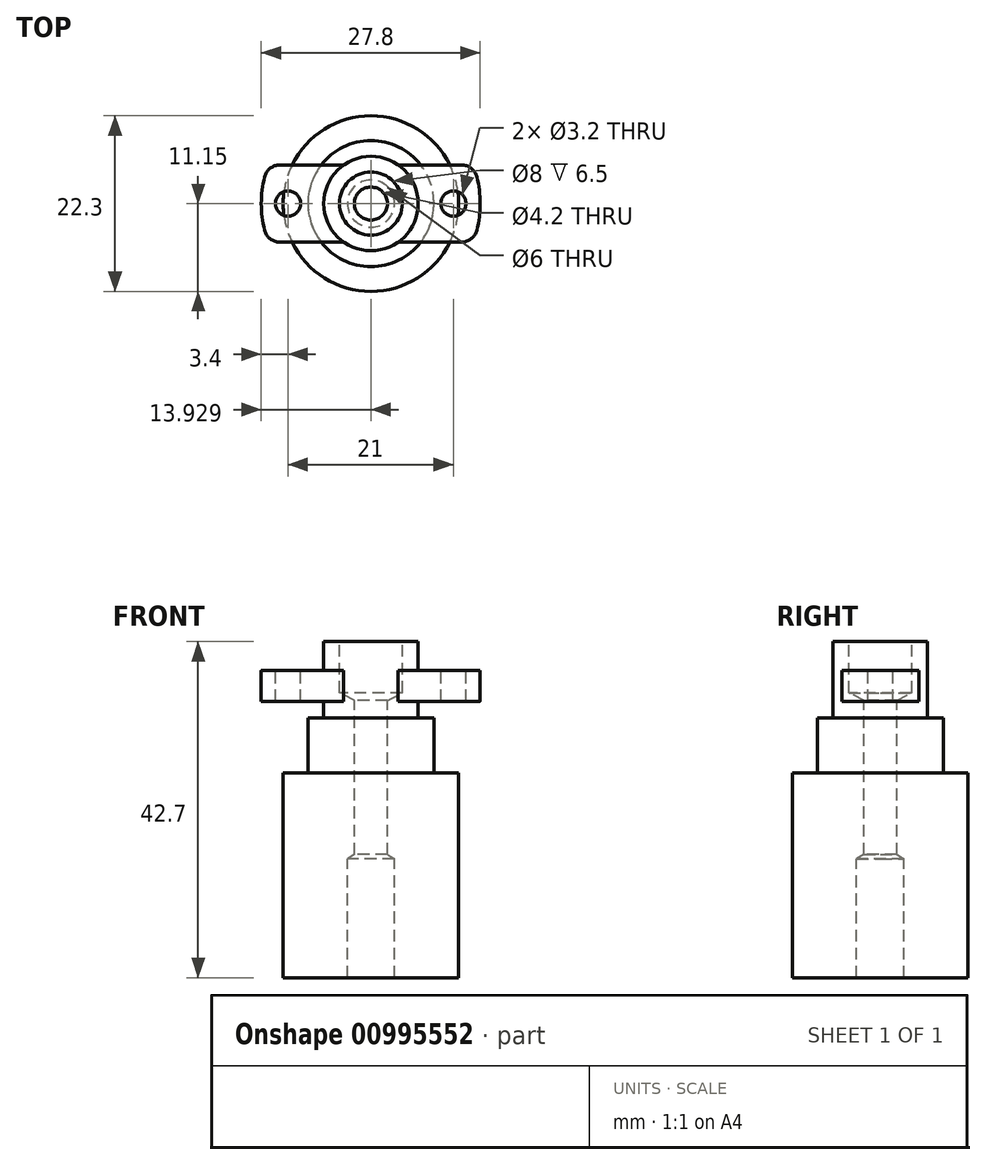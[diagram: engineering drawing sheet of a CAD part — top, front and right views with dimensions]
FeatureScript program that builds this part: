
annotation { "Feature Type Name" : "Feature", "Feature Type Description" : "" }
export const myFeature = defineFeature(function(context is Context, id is Id, definition is map)
    precondition{}
    {
        {
            var Q0;
            Q0=qCreatedBy(makeId("Front.planeOp"),FACE);
            var sketch = newSketch(context, id + "F0", { "sketchPlane" : qUnion([Q0])});
            skLineSegment(sketch, "E0", {"start": v(0.03, 24.7) * mm, "end": v(0.03, -18) * mm, "construction": true});
            skLineSegment(sketch, "E1", {"start": v(3.03, -18) * mm, "end": v(11.18, -18) * mm});
            skLineSegment(sketch, "E2", {"start": v(11.18, -18) * mm, "end": v(11.18, 8) * mm});
            skLineSegment(sketch, "E3", {"start": v(11.18, 8) * mm, "end": v(8.03, 8) * mm});
            skLineSegment(sketch, "E4", {"start": v(8.03, 8) * mm, "end": v(8.03, 15) * mm});
            skLineSegment(sketch, "E5", {"start": v(8.03, 15) * mm, "end": v(6.03, 15) * mm});
            skLineSegment(sketch, "E6", {"start": v(6.03, 15) * mm, "end": v(6.03, 21) * mm});
            skLineSegment(sketch, "E7", {"start": v(8.03, 21) * mm, "end": v(8.03, 24.7) * mm, "construction": true});
            skLineSegment(sketch, "E8", {"start": v(8.03, 24.7) * mm, "end": v(6.03, 24.7) * mm, "construction": true});
            skLineSegment(sketch, "E9", {"start": v(4.03, 24.7) * mm, "end": v(4.03, 18.2) * mm});
            skLineSegment(sketch, "E10", {"start": v(4.03, 18.2) * mm, "end": v(2.13, 17.18) * mm});
            skLineSegment(sketch, "E11", {"start": v(2.13, 17.18) * mm, "end": v(2.13, -2.36) * mm});
            skLineSegment(sketch, "E12", {"start": v(2.13, -2.36) * mm, "end": v(3.03, -2.9) * mm});
            skLineSegment(sketch, "E13", {"start": v(3.03, -2.9) * mm, "end": v(3.03, -18) * mm});
            skLineSegment(sketch, "E14", {"start": v(6.03, 21) * mm, "end": v(6.03, 24.7) * mm});
            skLineSegment(sketch, "E15", {"start": v(4.03, 24.7) * mm, "end": v(6.03, 24.7) * mm});
            skSolve(sketch);
        }
        {
            var Q0;
            Q0=makeQuery(id+"F0.imprint","IMPRINT",FACE,{"disambiguationData":[TD([[makeQuery(id+"F0.imprint","IMPRINT",EDGE,{"derivedFrom":sQuery(id+"F0.wireOp",EDGE,"E1")}),1.0]])]});
            var Q1;
            Q1=sQuery(id+"F0.wireOp",EDGE,"E0");
            revolve(context, id + "F1", {"surfaceOperationType" : NewSurfaceOperationType.NEW, "entities" : qUnion([Q0]), "axis" : qUnion([Q1]), "revolveType" : RevolveType.FULL});
        }
        {
            var Q0;
            Q0=makeQuery(id+"F1.opRevolve","SWEPT_FACE",FACE,{"disambiguationData":[OSD([sQuery(id+"F0.wireOp",EDGE,"E15")])]});
            cPlane(context, id + "F2", {"entities" : qUnion([Q0]), "cplaneType" : CPlaneType.OFFSET, "offset" : 3.7 * mm, "oppositeDirection" : true, "width" : 150 * mm, "height" : 150 * mm});
        }
        {
            var Q0;
            Q0=qCreatedBy(id+"F2.planeOp",FACE);
            var sketch = newSketch(context, id + "F3", { "sketchPlane" : qUnion([Q0])});
            skArc(sketch, "E16", {"start": v(-13.48, 3.39) * mm, "mid": v(-13.9, 0) * mm, "end": v(-13.48, -3.39) * mm});
            skLineSegment(sketch, "E17", {"start": v(-13.9, 0) * mm, "end": v(14.8, 0) * mm, "construction": true});
            skLineSegment(sketch, "E18.0", {"start": v(-11.54, -4.9) * mm, "end": v(11.54, -4.9) * mm});
            skLineSegment(sketch, "E19.0", {"start": v(-11.54, 4.9) * mm, "end": v(11.54, 4.9) * mm});
            skArc(sketch, "E20.trimOffspring", {"start": v(13.48, -3.39) * mm, "mid": v(13.9, 0) * mm, "end": v(13.48, 3.39) * mm});
            skPoint(sketch, "E21.visualSharp", {"position": v(-13, 4.9) * mm});
            skArc(sketch, "E21.filletArc", {"start": v(-11.54, 4.9) * mm, "mid": v(-12.77, 4.48) * mm, "end": v(-13.48, 3.39) * mm});
            skPoint(sketch, "E22.visualSharp", {"position": v(13, 4.9) * mm});
            skArc(sketch, "E22.filletArc", {"start": v(13.48, 3.39) * mm, "mid": v(12.77, 4.48) * mm, "end": v(11.54, 4.9) * mm});
            skPoint(sketch, "E23.visualSharp", {"position": v(13, -4.9) * mm});
            skArc(sketch, "E23.filletArc", {"start": v(11.54, -4.9) * mm, "mid": v(12.77, -4.48) * mm, "end": v(13.48, -3.39) * mm});
            skPoint(sketch, "E24.visualSharp", {"position": v(-13, -4.9) * mm});
            skArc(sketch, "E24.filletArc", {"start": v(-13.48, -3.39) * mm, "mid": v(-12.77, -4.48) * mm, "end": v(-11.54, -4.9) * mm});
            skCircle(sketch, "E25.0", {"center": v(0.03, 0) * mm, "radius": 4 * mm});
            skSolve(sketch);
        }
        {
            var Q0;
            Q0 = qSketchRegion(id + "F3", true);
            extrude(context, id + "F4", {"entities" : qUnion([Q0]), "operationType" : NewBodyOperationType.ADD, "oppositeDirection" : true, "depth" : 3.9 * mm, "offsetDistance" : 25 * mm});
        }
        {
            var Q0;
            {var subQ0=sQuery(id+"F3.wireOp",EDGE,"E18.0");var subQ1=sQuery(id+"F3.wireOp",EDGE,"E16");var subQ2=sQuery(id+"F3.wireOp",EDGE,"E19.0");var subQ3=sQuery(id+"F3.wireOp",EDGE,"E24.filletArc");var subQ4=sQuery(id+"F3.wireOp",EDGE,"E21.filletArc");Q0=makeQuery(id+"F4.boolean.opBoolean","SPLIT",FACE,{"disambiguationData":[TD([makeQuery(id+"F4.opExtrude","SWEPT_FACE",FACE,{"disambiguationData":[OSD([subQ1])]})])],"derivedFrom":makeQuery(id+"F4.opExtrude","CAP_FACE",FACE,{"disambiguationData":[OSD([subQ1,subQ0,subQ2,sQuery(id+"F3.wireOp",EDGE,"E20.trimOffspring"),subQ4,sQuery(id+"F3.wireOp",EDGE,"E22.filletArc"),sQuery(id+"F3.wireOp",EDGE,"E23.filletArc"),subQ3,sQuery(id+"F3.wireOp",EDGE,"E25.0")])],"isStart":true})});}
            var sketch = newSketch(context, id + "F5", { "sketchPlane" : qUnion([Q0])});
            skCircle(sketch, "E26", {"center": v(-10.5, 0) * mm, "radius": 1.6 * mm});
            skPoint(sketch, "E26.centerSnap0", {"position": v(-13.9, 0) * mm});
            skCircle(sketch, "E27", {"center": v(10.5, 0) * mm, "radius": 1.6 * mm});
            skLineSegment(sketch, "E28", {"start": v(0, 6.67) * mm, "end": v(0, -6.56) * mm, "construction": true});
            skSolve(sketch);
        }
        {
            var Q0;
            Q0=makeQuery(id+"F5.imprint","IMPRINT",FACE,{"disambiguationData":[TD([[makeQuery(id+"F5.imprint","IMPRINT",EDGE,{"derivedFrom":sQuery(id+"F5.wireOp",EDGE,"E26")}),1.0]])]});
            var Q1;
            Q1=makeQuery(id+"F5.imprint","IMPRINT",FACE,{"disambiguationData":[TD([[makeQuery(id+"F5.imprint","IMPRINT",EDGE,{"derivedFrom":sQuery(id+"F5.wireOp",EDGE,"E27")}),1.0]])]});
            extrude(context, id + "F6", {"entities" : qUnion([Q0, Q1]), "operationType" : NewBodyOperationType.REMOVE, "endBound" : BoundingType.UP_TO_NEXT, "oppositeDirection" : true, "depth" : 25 * mm, "offsetDistance" : 25 * mm});
        }
    });
